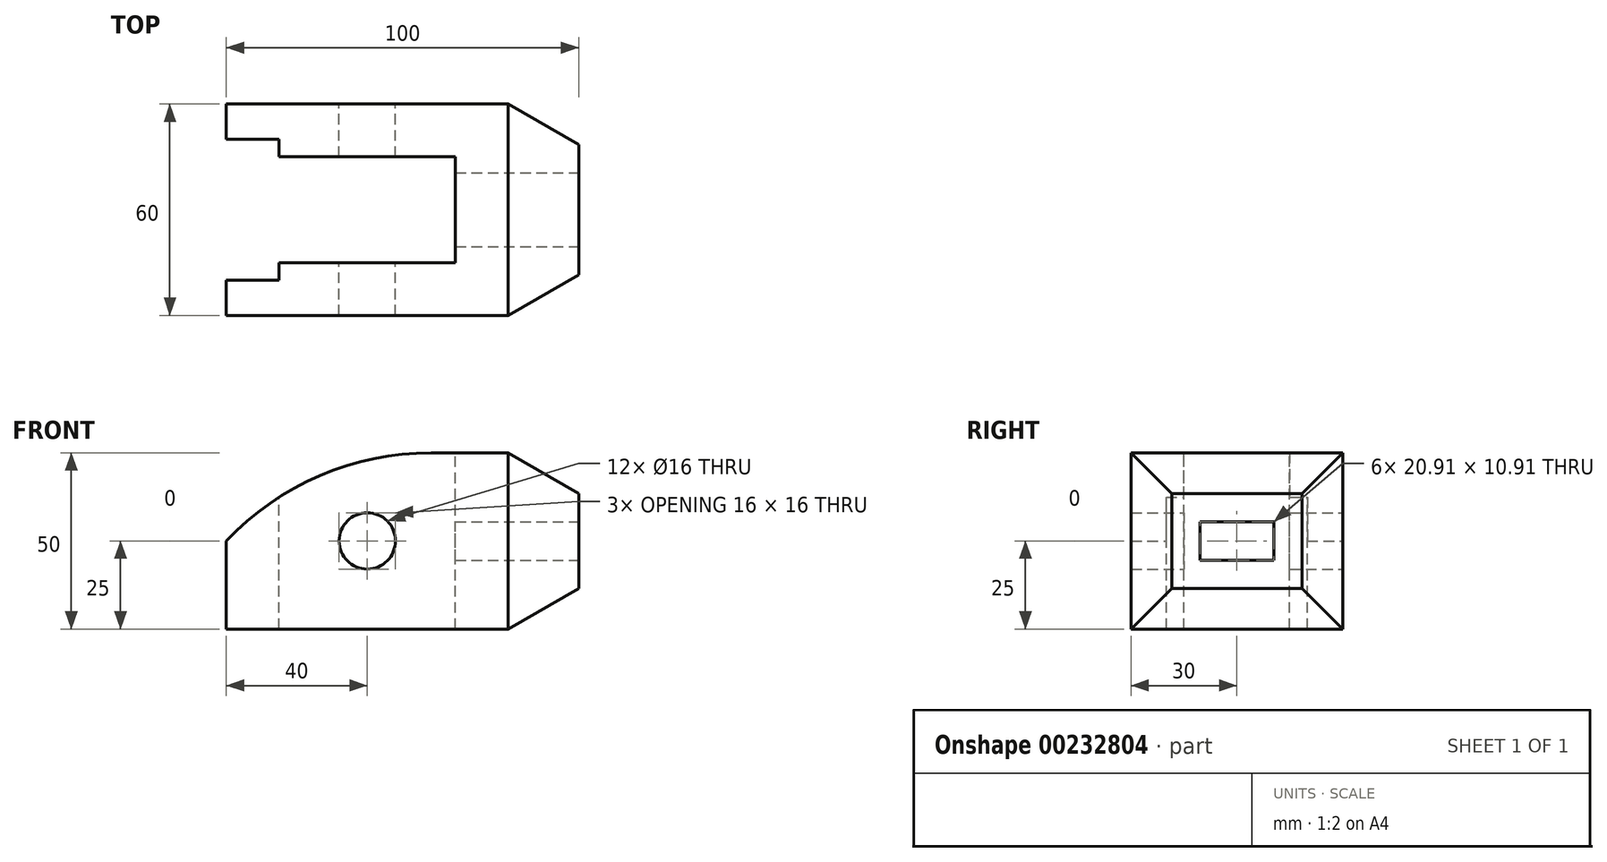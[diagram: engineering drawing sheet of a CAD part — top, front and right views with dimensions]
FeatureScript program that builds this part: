
annotation { "Feature Type Name" : "Feature", "Feature Type Description" : "" }
export const myFeature = defineFeature(function(context is Context, id is Id, definition is map)
    precondition{}
    {
        {
            var Q0;
            Q0=qCreatedBy(makeId("Front.planeOp"),FACE);
            var sketch = newSketch(context, id + "F0", { "sketchPlane" : qUnion([Q0])});
            skLineSegment(sketch, "E0", {"start": v(0, 0) * mm, "end": v(-80, 0) * mm});
            skLineSegment(sketch, "E1", {"start": v(-80, 0) * mm, "end": v(-80, 25) * mm});
            skLineSegment(sketch, "E2", {"start": v(-21.9, 50) * mm, "end": v(0, 50) * mm});
            skLineSegment(sketch, "E3", {"start": v(0, 50) * mm, "end": v(0, 0) * mm});
            skLineSegment(sketch, "E4", {"start": v(0, 0) * mm, "end": v(20, 11.55) * mm});
            skLineSegment(sketch, "E5", {"start": v(20, 11.55) * mm, "end": v(20, 38.45) * mm});
            skLineSegment(sketch, "E6", {"start": v(20, 38.45) * mm, "end": v(0, 50) * mm});
            skLineSegment(sketch, "E7", {"start": v(-98.53, 25) * mm, "end": v(72.06, 25) * mm, "construction": true});
            skArc(sketch, "E8", {"start": v(-80, 25) * mm, "mid": v(-53.53, 43.48) * mm, "end": v(-21.9, 50) * mm});
            skCircle(sketch, "E9", {"center": v(-40, 25) * mm, "radius": 8 * mm});
            skSolve(sketch);
        }
        {
            var Q0;
            Q0=makeQuery(id+"F0.imprint","IMPRINT",FACE,{"disambiguationData":[TD([[makeQuery(id+"F0.imprint","IMPRINT",EDGE,{"derivedFrom":sQuery(id+"F0.wireOp",EDGE,"E0")}),-1.0]])]});
            var Q1;
            Q1=makeQuery(id+"F0.imprint","IMPRINT",FACE,{"disambiguationData":[TD([[makeQuery(id+"F0.imprint","IMPRINT",EDGE,{"derivedFrom":sQuery(id+"F0.wireOp",EDGE,"E3")}),1.0]])]});
            extrude(context, id + "F1", {"entities" : qUnion([Q0, Q1]), "depth" : 60 * mm});
        }
        {
            var Q0;
            Q0=makeQuery(id+"F1.opExtrude","SWEPT_FACE",FACE,{"disambiguationData":[OSD([sQuery(id+"F0.wireOp",EDGE,"E2")])]});
            var sketch = newSketch(context, id + "F2", { "sketchPlane" : qUnion([Q0])});
            skLineSegment(sketch, "E10.0.0", {"start": v(-21.9, 0) * mm, "end": v(-80, 0) * mm, "construction": true});
            skLineSegment(sketch, "E10.0.1", {"start": v(-80, 0) * mm, "end": v(-80, -60) * mm, "construction": true});
            skLineSegment(sketch, "E10.0.2", {"start": v(-80, -60) * mm, "end": v(-21.9, -60) * mm, "construction": true});
            skLineSegment(sketch, "E10.0.3", {"start": v(-21.9, -60) * mm, "end": v(-21.9, 0) * mm, "construction": true});
            skLineSegment(sketch, "E11.0.0", {"start": v(0, 0) * mm, "end": v(-21.9, 0) * mm, "construction": true});
            skLineSegment(sketch, "E11.0.1", {"start": v(-21.9, 0) * mm, "end": v(-21.9, -60) * mm, "construction": true});
            skLineSegment(sketch, "E11.0.2", {"start": v(-21.9, -60) * mm, "end": v(0, -60) * mm, "construction": true});
            skLineSegment(sketch, "E11.0.3", {"start": v(0, -60) * mm, "end": v(0, 0) * mm, "construction": true});
            skLineSegment(sketch, "E12.0.0", {"start": v(20, 0) * mm, "end": v(0, 0) * mm, "construction": true});
            skLineSegment(sketch, "E12.0.1", {"start": v(0, 0) * mm, "end": v(0, -60) * mm, "construction": true});
            skLineSegment(sketch, "E12.0.2", {"start": v(0, -60) * mm, "end": v(20, -60) * mm, "construction": true});
            skLineSegment(sketch, "E12.0.3", {"start": v(20, -60) * mm, "end": v(20, 0) * mm, "construction": true});
            skLineSegment(sketch, "E13", {"start": v(-80, -10) * mm, "end": v(-65, -10) * mm});
            skLineSegment(sketch, "E14", {"start": v(-65, -10) * mm, "end": v(-65, -15) * mm});
            skLineSegment(sketch, "E15", {"start": v(-65, -15) * mm, "end": v(-15, -15) * mm});
            skLineSegment(sketch, "E16", {"start": v(-15, -15) * mm, "end": v(-15, -45) * mm});
            skLineSegment(sketch, "E17", {"start": v(-15, -45) * mm, "end": v(-65, -45) * mm});
            skLineSegment(sketch, "E18", {"start": v(-65, -45) * mm, "end": v(-65, -50) * mm});
            skLineSegment(sketch, "E19", {"start": v(-65, -50) * mm, "end": v(-80, -50) * mm});
            skLineSegment(sketch, "E20", {"start": v(-80, -50) * mm, "end": v(-80, -10) * mm});
            skLineSegment(sketch, "E21", {"start": v(0, 0) * mm, "end": v(20, -11.55) * mm});
            skLineSegment(sketch, "E22", {"start": v(20, -11.55) * mm, "end": v(20, 0) * mm});
            skLineSegment(sketch, "E23", {"start": v(20, 0) * mm, "end": v(20, -11.55) * mm});
            skLineSegment(sketch, "E24", {"start": v(20, 0) * mm, "end": v(0, 0) * mm});
            skLineSegment(sketch, "E25", {"start": v(0, -60) * mm, "end": v(20, -48.45) * mm});
            skLineSegment(sketch, "E26", {"start": v(20, -48.45) * mm, "end": v(20, -60) * mm});
            skLineSegment(sketch, "E27", {"start": v(0, -60) * mm, "end": v(20, -60) * mm});
            skSolve(sketch);
        }
        {
            var Q0;
            Q0=makeQuery(id+"F2.imprint","IMPRINT",FACE,{"disambiguationData":[TD([[makeQuery(id+"F2.imprint","IMPRINT",EDGE,{"derivedFrom":sQuery(id+"F2.wireOp",EDGE,"E13")}),-1.0]])]});
            var Q1;
            {var subQ0=sQuery(id+"F2.wireOp",EDGE,"E16");Q1=makeQuery(id+"F2.imprint","IMPRINT",FACE,{"disambiguationData":[TD([[makeQuery(id+"F2.imprint","IMPRINT",EDGE,{"derivedFrom":subQ0}),-1.0]])]});}
            var Q2;
            Q2=makeQuery(id+"F2.imprint","IMPRINT",FACE,{"disambiguationData":[TD([[makeQuery(id+"F2.imprint","IMPRINT",EDGE,{"derivedFrom":sQuery(id+"F2.wireOp",EDGE,"E21")}),1.0]])]});
            var Q3;
            Q3=makeQuery(id+"F2.imprint","IMPRINT",FACE,{"disambiguationData":[TD([[makeQuery(id+"F2.imprint","IMPRINT",EDGE,{"derivedFrom":sQuery(id+"F2.wireOp",EDGE,"E25")}),-1.0]])]});
            extrude(context, id + "F3", {"entities" : qUnion([Q0, Q1, Q2, Q3]), "operationType" : NewBodyOperationType.REMOVE, "endBound" : BoundingType.THROUGH_ALL, "oppositeDirection" : true, "depth" : 25 * mm});
        }
        {
            var Q0;
            Q0=makeQuery(id+"F1.opExtrude","SWEPT_FACE",FACE,{"disambiguationData":[OSD([sQuery(id+"F0.wireOp",EDGE,"E5")])]});
            var sketch = newSketch(context, id + "F4", { "sketchPlane" : qUnion([Q0])});
            skLineSegment(sketch, "E28.0.0", {"start": v(-48.45, 38.45) * mm, "end": v(-48.45, 11.55) * mm, "construction": true});
            skLineSegment(sketch, "E28.0.1", {"start": v(-48.45, 11.55) * mm, "end": v(-11.55, 11.55) * mm, "construction": true});
            skLineSegment(sketch, "E28.0.2", {"start": v(-11.55, 11.55) * mm, "end": v(-11.55, 38.45) * mm, "construction": true});
            skLineSegment(sketch, "E28.0.3", {"start": v(-11.55, 38.45) * mm, "end": v(-48.45, 38.45) * mm, "construction": true});
            skLineSegment(sketch, "E29", {"start": v(-72.3, 25) * mm, "end": v(10.15, 25) * mm, "construction": true});
            skLineSegment(sketch, "E30", {"start": v(-30, 60.5) * mm, "end": v(-30, -6.92) * mm, "construction": true});
            skPoint(sketch, "E31", {"position": v(-30, 38.45) * mm});
            skPoint(sketch, "E32", {"position": v(-11.55, 25) * mm});
            skLineSegment(sketch, "E33.bottom", {"start": v(-40.45, 30.45) * mm, "end": v(-19.55, 30.45) * mm});
            skLineSegment(sketch, "E33.top", {"start": v(-40.45, 19.55) * mm, "end": v(-19.55, 19.55) * mm});
            skLineSegment(sketch, "E33.left", {"start": v(-40.45, 30.45) * mm, "end": v(-40.45, 19.55) * mm});
            skLineSegment(sketch, "E33.right", {"start": v(-19.55, 30.45) * mm, "end": v(-19.55, 19.55) * mm});
            skPoint(sketch, "E33.middle", {"position": v(-30, 25) * mm});
            skSolve(sketch);
        }
        {
            var Q0;
            Q0=makeQuery(id+"F4.imprint","IMPRINT",FACE,{"disambiguationData":[TD([[makeQuery(id+"F4.imprint","IMPRINT",EDGE,{"derivedFrom":sQuery(id+"F4.wireOp",EDGE,"E33.bottom")}),-1.0]])]});
            extrude(context, id + "F5", {"entities" : qUnion([Q0]), "operationType" : NewBodyOperationType.REMOVE, "endBound" : BoundingType.THROUGH_ALL, "oppositeDirection" : true, "depth" : 25 * mm});
        }
    });
